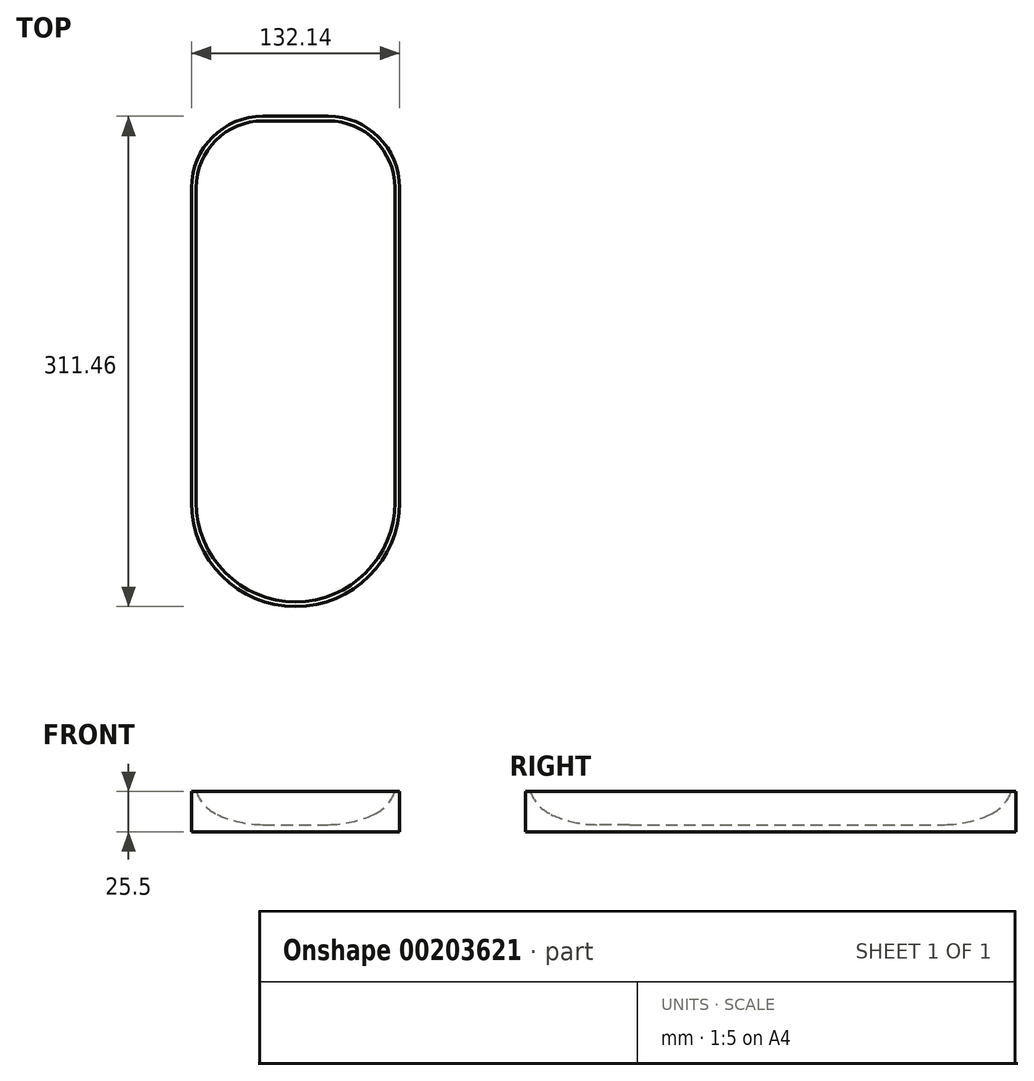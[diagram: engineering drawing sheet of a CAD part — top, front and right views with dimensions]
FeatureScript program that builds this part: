
annotation { "Feature Type Name" : "Feature", "Feature Type Description" : "" }
export const myFeature = defineFeature(function(context is Context, id is Id, definition is map)
    precondition{}
    {
        {
            var Q0;
            Q0=qCreatedBy(makeId("Front.planeOp"),FACE);
            var sketch = newSketch(context, id + "F0", { "sketchPlane" : qUnion([Q0])});
            skArc(sketch, "E0", {"start": v(20.67, 0) * mm, "mid": v(35.7, 1.67) * mm, "end": v(50, 6.59) * mm});
            skArc(sketch, "E1", {"start": v(50, 6.59) * mm, "mid": v(57.97, 12.5) * mm, "end": v(63.07, 21.03) * mm});
            skLineSegment(sketch, "E2", {"start": v(63.07, 21.03) * mm, "end": v(66.07, 21.03) * mm});
            skLineSegment(sketch, "E3", {"start": v(66.07, 21.03) * mm, "end": v(66.07, -4.47) * mm});
            skLineSegment(sketch, "E4", {"start": v(66.07, -4.47) * mm, "end": v(0, -4.47) * mm});
            skLineSegment(sketch, "E5", {"start": v(0, -4.47) * mm, "end": v(0, 0) * mm});
            skLineSegment(sketch, "E6", {"start": v(0, 0) * mm, "end": v(20.67, 0) * mm});
            skSolve(sketch);
        }
        {
            var Q0;
            Q0 = qSketchRegion(id + "F0", true);
            extrude(context, id + "F1", {"entities" : qUnion([Q0]), "endBound" : BoundingType.SYMMETRIC, "depth" : 200 * mm});
        }
        {
            var Q0;
            Q0=makeQuery(id+"F1.opExtrude","CAP_FACE",FACE,{"disambiguationData":[OSD([sQuery(id+"F0.wireOp",EDGE,"E0"),sQuery(id+"F0.wireOp",EDGE,"E1"),sQuery(id+"F0.wireOp",EDGE,"E2"),sQuery(id+"F0.wireOp",EDGE,"E3"),sQuery(id+"F0.wireOp",EDGE,"E4"),sQuery(id+"F0.wireOp",EDGE,"E5"),sQuery(id+"F0.wireOp",EDGE,"E6")])],"isStart":false});
            var Q1;
            Q1=makeQuery(id+"F1.opExtrude","CAP_EDGE",EDGE,{"disambiguationData":[OSD([sQuery(id+"F0.wireOp",EDGE,"E5")])],"isStart":false});
            revolve(context, id + "F2", {"operationType" : NewBodyOperationType.ADD, "entities" : qUnion([Q0]), "axis" : qUnion([Q1]), "revolveType" : RevolveType.ONE_DIRECTION, "oppositeDirection" : true, "angle" : 90 * degree});
        }
        {
            var Q0;
            Q0=makeQuery(id+"F1.opExtrude","CAP_FACE",FACE,{"disambiguationData":[OSD([sQuery(id+"F0.wireOp",EDGE,"E0"),sQuery(id+"F0.wireOp",EDGE,"E1"),sQuery(id+"F0.wireOp",EDGE,"E2"),sQuery(id+"F0.wireOp",EDGE,"E3"),sQuery(id+"F0.wireOp",EDGE,"E4"),sQuery(id+"F0.wireOp",EDGE,"E5"),sQuery(id+"F0.wireOp",EDGE,"E6")])],"isStart":true});
            var sketch = newSketch(context, id + "F3", { "sketchPlane" : qUnion([Q0])});
            skLineSegment(sketch, "E7.0", {"start": v(-66.07, 21.03) * mm, "end": v(-66.07, -4.47) * mm});
            skLineSegment(sketch, "E7.1", {"start": v(-63.07, 21.03) * mm, "end": v(-66.07, 21.03) * mm});
            skArc(sketch, "E7.2", {"start": v(-50, 6.59) * mm, "mid": v(-57.97, 12.5) * mm, "end": v(-63.07, 21.03) * mm});
            skArc(sketch, "E7.3", {"start": v(-20.67, 0) * mm, "mid": v(-35.7, 1.67) * mm, "end": v(-50, 6.59) * mm});
            skLineSegment(sketch, "E8", {"start": v(-20.67, 0) * mm, "end": v(-20.67, -4.47) * mm});
            skLineSegment(sketch, "E9", {"start": v(-20.67, -4.47) * mm, "end": v(-66.07, -4.47) * mm});
            skSolve(sketch);
        }
        {
            var Q0;
            Q0=makeQuery(id+"F3.imprint","IMPRINT",FACE,{"disambiguationData":[TD([[makeQuery(id+"F3.imprint","IMPRINT",EDGE,{"derivedFrom":sQuery(id+"F3.wireOp",EDGE,"E7.0")}),1.0]])]});
            var Q1;
            Q1=sQuery(id+"F3.wireOp",EDGE,"E8");
            revolve(context, id + "F4", {"operationType" : NewBodyOperationType.ADD, "entities" : qUnion([Q0]), "axis" : qUnion([Q1]), "revolveType" : RevolveType.ONE_DIRECTION, "oppositeDirection" : true, "angle" : 90 * degree});
        }
        {
            var Q0;
            Q0=makeQuery(id+"F4.opRevolve","CAP_FACE",FACE,{"disambiguationData":[OSD([sQuery(id+"F3.wireOp",EDGE,"E7.0"),sQuery(id+"F3.wireOp",EDGE,"E7.1"),sQuery(id+"F3.wireOp",EDGE,"E7.2"),sQuery(id+"F3.wireOp",EDGE,"E7.3"),sQuery(id+"F3.wireOp",EDGE,"E8"),sQuery(id+"F3.wireOp",EDGE,"E9")])],"isStart":false});
            var Q1;
            {var subQ0=sQuery(id+"F0.wireOp",EDGE,"E5");Q1=makeQuery(id+"F2.boolean.opBoolean","MERGE",FACE,{"derivedFrom":[makeQuery(id+"F1.opExtrude","SWEPT_FACE",FACE,{"disambiguationData":[OSD([subQ0])]}),makeQuery(id+"F2.opRevolve","CAP_FACE",FACE,{"disambiguationData":[OSD([sQuery(id+"F0.wireOp",EDGE,"E0"),sQuery(id+"F0.wireOp",EDGE,"E1"),sQuery(id+"F0.wireOp",EDGE,"E2"),sQuery(id+"F0.wireOp",EDGE,"E3"),sQuery(id+"F0.wireOp",EDGE,"E4"),subQ0,sQuery(id+"F0.wireOp",EDGE,"E6")])],"isStart":false})]});}
            extrude(context, id + "F5", {"entities" : qUnion([Q0]), "operationType" : NewBodyOperationType.ADD, "endBound" : BoundingType.UP_TO_SURFACE, "endBoundEntityFace" : qUnion([Q1]), "depth" : 25 * mm});
        }
        {
            var Q0;
            Q0=makeQuery(id+"F1.opExtrude","SWEPT_BODY",BODY,{"disambiguationData":[OSD([sQuery(id+"F0.wireOp",EDGE,"E0"),sQuery(id+"F0.wireOp",EDGE,"E1"),sQuery(id+"F0.wireOp",EDGE,"E2"),sQuery(id+"F0.wireOp",EDGE,"E3"),sQuery(id+"F0.wireOp",EDGE,"E4"),sQuery(id+"F0.wireOp",EDGE,"E5"),sQuery(id+"F0.wireOp",EDGE,"E6")])]});
            var Q1;
            {var subQ0=sQuery(id+"F0.wireOp",EDGE,"E5");Q1=makeQuery(id+"F2.boolean.opBoolean","MERGE",FACE,{"derivedFrom":[makeQuery(id+"F1.opExtrude","SWEPT_FACE",FACE,{"disambiguationData":[OSD([subQ0])]}),makeQuery(id+"F2.opRevolve","CAP_FACE",FACE,{"disambiguationData":[OSD([sQuery(id+"F0.wireOp",EDGE,"E0"),sQuery(id+"F0.wireOp",EDGE,"E1"),sQuery(id+"F0.wireOp",EDGE,"E2"),sQuery(id+"F0.wireOp",EDGE,"E3"),sQuery(id+"F0.wireOp",EDGE,"E4"),subQ0,sQuery(id+"F0.wireOp",EDGE,"E6")])],"isStart":false})]});}
            mirror(context, id + "F6", {"operationType" : NewBodyOperationType.ADD, "entities" : qUnion([Q0]), "mirrorPlane" : qUnion([Q1])});
        }
    });
